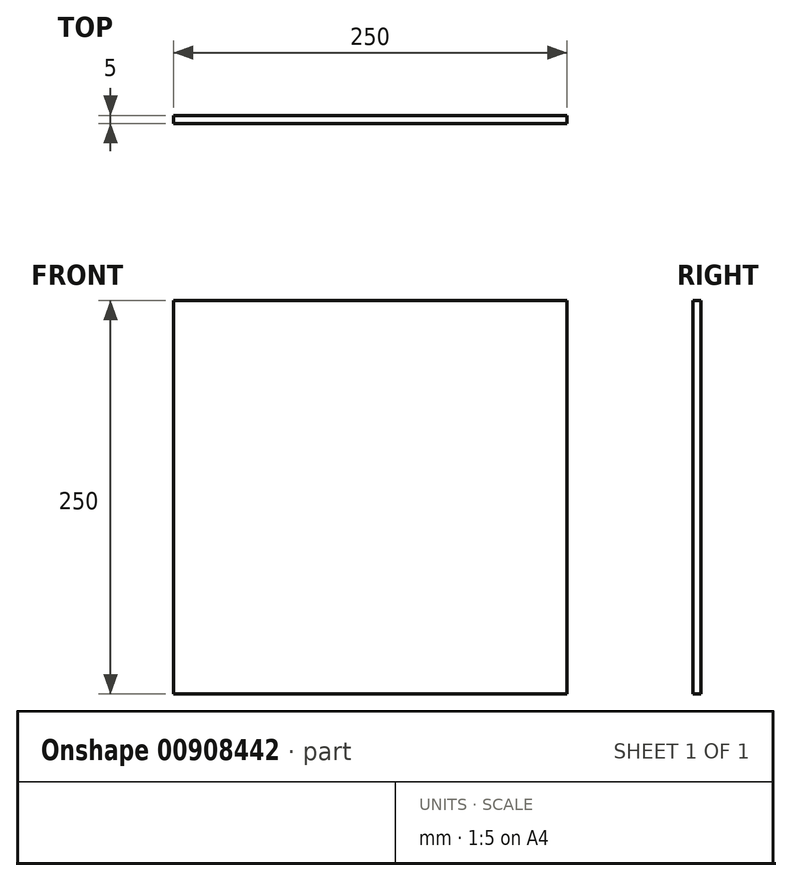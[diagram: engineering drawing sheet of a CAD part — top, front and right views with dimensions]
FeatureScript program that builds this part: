
annotation { "Feature Type Name" : "Feature", "Feature Type Description" : "" }
export const myFeature = defineFeature(function(context is Context, id is Id, definition is map)
    precondition{}
    {
        {
            var Q0;
            Q0=qCreatedBy(makeId("Front.planeOp"),FACE);
            var sketch = newSketch(context, id + "F0", { "sketchPlane" : qUnion([Q0])});
            skLineSegment(sketch, "E0.bottom", {"start": v(125, -125) * mm, "end": v(-125, -125) * mm});
            skLineSegment(sketch, "E0.top", {"start": v(125, 125) * mm, "end": v(-125, 125) * mm});
            skLineSegment(sketch, "E0.left", {"start": v(125, -125) * mm, "end": v(125, 125) * mm});
            skLineSegment(sketch, "E0.right", {"start": v(-125, -125) * mm, "end": v(-125, 125) * mm});
            skPoint(sketch, "E0.middle", {"position": v(0, 0) * mm});
            skSolve(sketch);
        }
        {
            var Q0;
            Q0 = qSketchRegion(id + "F0", true);
            extrude(context, id + "F1", {"entities" : qUnion([Q0]), "depth" : 5 * mm, "offsetDistance" : 25.4 * mm});
        }
    });
